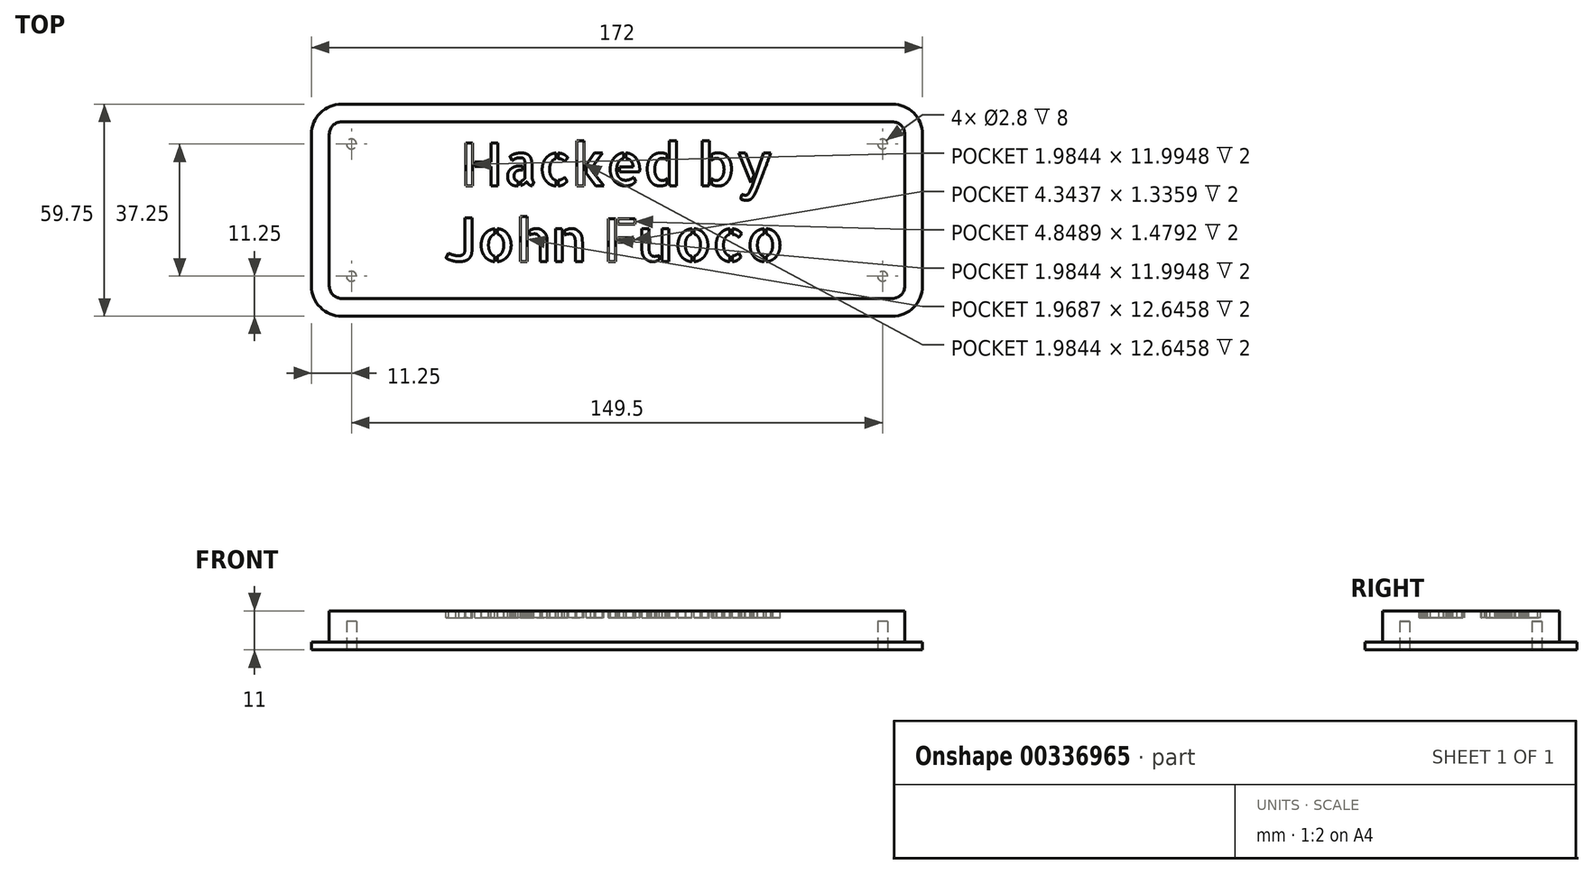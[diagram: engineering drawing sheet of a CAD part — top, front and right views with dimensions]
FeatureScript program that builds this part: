
annotation { "Feature Type Name" : "Feature", "Feature Type Description" : "" }
export const myFeature = defineFeature(function(context is Context, id is Id, definition is map)
    precondition{}
    {
        {
            var Q0;
            Q0=qCreatedBy(makeId("Top.planeOp"),FACE);
            var sketch = newSketch(context, id + "F0", { "sketchPlane" : qUnion([Q0])});
            skLineSegment(sketch, "E0.bottom", {"start": v(3.5, 0) * mm, "end": v(158.5, 0) * mm});
            skLineSegment(sketch, "E0.top", {"start": v(3.5, 49.75) * mm, "end": v(158.5, 49.75) * mm});
            skLineSegment(sketch, "E0.left", {"start": v(0, 3.5) * mm, "end": v(0, 46.25) * mm});
            skLineSegment(sketch, "E0.right", {"start": v(162, 3.5) * mm, "end": v(162, 46.25) * mm});
            skPoint(sketch, "E1.visualSharp", {"position": v(0, 49.75) * mm});
            skArc(sketch, "E1.filletArc", {"start": v(3.5, 49.75) * mm, "mid": v(1.03, 48.72) * mm, "end": v(0, 46.25) * mm});
            skPoint(sketch, "E2.visualSharp", {"position": v(162, 49.75) * mm});
            skArc(sketch, "E2.filletArc", {"start": v(162, 46.25) * mm, "mid": v(160.97, 48.72) * mm, "end": v(158.5, 49.75) * mm});
            skPoint(sketch, "E3.visualSharp", {"position": v(162, 0) * mm});
            skArc(sketch, "E3.filletArc", {"start": v(158.5, 0) * mm, "mid": v(160.97, 1.03) * mm, "end": v(162, 3.5) * mm});
            skPoint(sketch, "E4.visualSharp", {"position": v(0, 0) * mm});
            skArc(sketch, "E4.filletArc", {"start": v(0, 3.5) * mm, "mid": v(1.03, 1.03) * mm, "end": v(3.5, 0) * mm});
            skArc(sketch, "E5.0", {"start": v(3.5, 54.75) * mm, "mid": v(-2.51, 52.26) * mm, "end": v(-5, 46.25) * mm});
            skLineSegment(sketch, "E5.1", {"start": v(-5, 3.5) * mm, "end": v(-5, 46.25) * mm});
            skLineSegment(sketch, "E5.2", {"start": v(3.5, 54.75) * mm, "end": v(158.5, 54.75) * mm});
            skArc(sketch, "E5.3", {"start": v(-5, 3.5) * mm, "mid": v(-2.51, -2.51) * mm, "end": v(3.5, -5) * mm});
            skArc(sketch, "E5.4", {"start": v(167, 46.25) * mm, "mid": v(164.51, 52.26) * mm, "end": v(158.5, 54.75) * mm});
            skLineSegment(sketch, "E5.5", {"start": v(167, 3.5) * mm, "end": v(167, 46.25) * mm});
            skArc(sketch, "E5.6", {"start": v(158.5, -5) * mm, "mid": v(164.51, -2.51) * mm, "end": v(167, 3.5) * mm});
            skLineSegment(sketch, "E5.7", {"start": v(3.5, -5) * mm, "end": v(158.5, -5) * mm});
            skCircle(sketch, "E6", {"center": v(6.25, 6.25) * mm, "radius": 1.4 * mm});
            skCircle(sketch, "E7", {"center": v(6.25, 43.5) * mm, "radius": 1.4 * mm});
            skCircle(sketch, "E8", {"center": v(155.75, 43.5) * mm, "radius": 1.4 * mm});
            skCircle(sketch, "E9", {"center": v(155.75, 6.25) * mm, "radius": 1.4 * mm});
            skSolve(sketch);
        }
        {
            var Q0;
            Q0=makeQuery(id+"F0.imprint","IMPRINT",FACE,{"disambiguationData":[TD([[makeQuery(id+"F0.imprint","IMPRINT",EDGE,{"derivedFrom":sQuery(id+"F0.wireOp",EDGE,"E0.bottom")}),1.0]])]});
            extrude(context, id + "F1", {"entities" : qUnion([Q0]), "depth" : 11 * mm});
        }
        {
            var Q0;
            Q0=makeQuery(id+"F0.imprint","IMPRINT",FACE,{"disambiguationData":[TD([[makeQuery(id+"F0.imprint","IMPRINT",EDGE,{"derivedFrom":sQuery(id+"F0.wireOp",EDGE,"E0.bottom")}),-1.0]])]});
            extrude(context, id + "F2", {"entities" : qUnion([Q0]), "operationType" : NewBodyOperationType.ADD, "depth" : 2.2 * mm});
        }
        {
            var Q0;
            Q0=makeQuery(id+"F0.imprint","IMPRINT",FACE,{"disambiguationData":[TD([[makeQuery(id+"F0.imprint","IMPRINT",EDGE,{"derivedFrom":sQuery(id+"F0.wireOp",EDGE,"E7")}),1.0]])]});
            var Q1;
            Q1=makeQuery(id+"F0.imprint","IMPRINT",FACE,{"disambiguationData":[TD([[makeQuery(id+"F0.imprint","IMPRINT",EDGE,{"derivedFrom":sQuery(id+"F0.wireOp",EDGE,"E6")}),1.0]])]});
            var Q2;
            Q2=makeQuery(id+"F0.imprint","IMPRINT",FACE,{"disambiguationData":[TD([[makeQuery(id+"F0.imprint","IMPRINT",EDGE,{"derivedFrom":sQuery(id+"F0.wireOp",EDGE,"E9")}),1.0]])]});
            var Q3;
            Q3=makeQuery(id+"F0.imprint","IMPRINT",FACE,{"disambiguationData":[TD([[makeQuery(id+"F0.imprint","IMPRINT",EDGE,{"derivedFrom":sQuery(id+"F0.wireOp",EDGE,"E8")}),1.0]])]});
            extrude(context, id + "F3", {"entities" : qUnion([Q0, Q1, Q2, Q3]), "operationType" : NewBodyOperationType.ADD, "depth" : 11 * mm, "hasSecondDirection" : true, "secondDirectionOppositeDirection" : false, "secondDirectionDepth" : 8 * mm});
        }
        {
            var Q0;
            {var subQ0=sQuery(id+"F0.wireOp",EDGE,"E9");var subQ1=sQuery(id+"F0.wireOp",EDGE,"E8");var subQ2=sQuery(id+"F0.wireOp",EDGE,"E7");var subQ3=sQuery(id+"F0.wireOp",EDGE,"E6");Q0=makeQuery(id+"F3.boolean.opBoolean","MERGE",FACE,{"derivedFrom":[makeQuery(id+"F1.opExtrude","CAP_FACE",FACE,{"disambiguationData":[OSD([sQuery(id+"F0.wireOp",EDGE,"E0.bottom"),sQuery(id+"F0.wireOp",EDGE,"E0.top"),sQuery(id+"F0.wireOp",EDGE,"E0.left"),sQuery(id+"F0.wireOp",EDGE,"E0.right"),sQuery(id+"F0.wireOp",EDGE,"E1.filletArc"),sQuery(id+"F0.wireOp",EDGE,"E2.filletArc"),sQuery(id+"F0.wireOp",EDGE,"E3.filletArc"),sQuery(id+"F0.wireOp",EDGE,"E4.filletArc"),subQ3,subQ2,subQ1,subQ0])],"isStart":false}),makeQuery(id+"F3.opExtrude","CAP_FACE",FACE,{"disambiguationData":[OSD([subQ3])],"isStart":false}),makeQuery(id+"F3.opExtrude","CAP_FACE",FACE,{"disambiguationData":[OSD([subQ2])],"isStart":false}),makeQuery(id+"F3.opExtrude","CAP_FACE",FACE,{"disambiguationData":[OSD([subQ1])],"isStart":false}),makeQuery(id+"F3.opExtrude","CAP_FACE",FACE,{"disambiguationData":[OSD([subQ0])],"isStart":false})]});}
            var sketch = newSketch(context, id + "F4", { "sketchPlane" : qUnion([Q0])});
            skText(sketch, "E10", { "text": " Hacked by\nJohn Fuoco", "fontName": "AllertaStencil-Regular.ttf"});
            const initialGuessF4  = {"E10": [0.03238, 0.03175, 1, 0, 0.012]};
            skSetInitialGuess(sketch, initialGuessF4);
            skSolve(sketch);
        }
        {
            var Q0;
            Q0=makeQuery(id+"F4.imprint","IMPRINT",FACE,{"disambiguationData":[TD([[makeQuery(id+"F4.imprint","IMPRINT",EDGE,{"derivedFrom":sQuery(id+"F4.wireOp",EDGE,"E10.sketch_text.stroke-8")}),-1.0]])]});
            var Q1;
            Q1=makeQuery(id+"F4.imprint","IMPRINT",FACE,{"disambiguationData":[TD([[makeQuery(id+"F4.imprint","IMPRINT",EDGE,{"derivedFrom":sQuery(id+"F4.wireOp",EDGE,"E10.sketch_text.stroke-0")}),-1.0]])]});
            var Q2;
            Q2=makeQuery(id+"F4.imprint","IMPRINT",FACE,{"disambiguationData":[TD([[makeQuery(id+"F4.imprint","IMPRINT",EDGE,{"derivedFrom":sQuery(id+"F4.wireOp",EDGE,"E10.sketch_text.stroke-31")}),-1.0]])]});
            var Q3;
            Q3=makeQuery(id+"F4.imprint","IMPRINT",FACE,{"disambiguationData":[TD([[makeQuery(id+"F4.imprint","IMPRINT",EDGE,{"derivedFrom":sQuery(id+"F4.wireOp",EDGE,"E10.sketch_text.stroke-12")}),-1.0]])]});
            var Q4;
            Q4=makeQuery(id+"F4.imprint","IMPRINT",FACE,{"disambiguationData":[TD([[makeQuery(id+"F4.imprint","IMPRINT",EDGE,{"derivedFrom":sQuery(id+"F4.wireOp",EDGE,"E10.sketch_text.stroke-79")}),-1.0]])]});
            var Q5;
            Q5=makeQuery(id+"F4.imprint","IMPRINT",FACE,{"disambiguationData":[TD([[makeQuery(id+"F4.imprint","IMPRINT",EDGE,{"derivedFrom":sQuery(id+"F4.wireOp",EDGE,"E10.sketch_text.stroke-67")}),-1.0]])]});
            var Q6;
            Q6=makeQuery(id+"F4.imprint","IMPRINT",FACE,{"disambiguationData":[TD([[makeQuery(id+"F4.imprint","IMPRINT",EDGE,{"derivedFrom":sQuery(id+"F4.wireOp",EDGE,"E10.sketch_text.stroke-73")}),-1.0]])]});
            var Q7;
            Q7=makeQuery(id+"F4.imprint","IMPRINT",FACE,{"disambiguationData":[TD([[makeQuery(id+"F4.imprint","IMPRINT",EDGE,{"derivedFrom":sQuery(id+"F4.wireOp",EDGE,"E10.sketch_text.stroke-102")}),-1.0]])]});
            var Q8;
            Q8=makeQuery(id+"F4.imprint","IMPRINT",FACE,{"disambiguationData":[TD([[makeQuery(id+"F4.imprint","IMPRINT",EDGE,{"derivedFrom":sQuery(id+"F4.wireOp",EDGE,"E10.sketch_text.stroke-95")}),-1.0]])]});
            var Q9;
            Q9=makeQuery(id+"F4.imprint","IMPRINT",FACE,{"disambiguationData":[TD([[makeQuery(id+"F4.imprint","IMPRINT",EDGE,{"derivedFrom":sQuery(id+"F4.wireOp",EDGE,"E10.sketch_text.stroke-119")}),-1.0]])]});
            var Q10;
            Q10=makeQuery(id+"F4.imprint","IMPRINT",FACE,{"disambiguationData":[TD([[makeQuery(id+"F4.imprint","IMPRINT",EDGE,{"derivedFrom":sQuery(id+"F4.wireOp",EDGE,"E10.sketch_text.stroke-106")}),-1.0]])]});
            var Q11;
            Q11=makeQuery(id+"F4.imprint","IMPRINT",FACE,{"disambiguationData":[TD([[makeQuery(id+"F4.imprint","IMPRINT",EDGE,{"derivedFrom":sQuery(id+"F4.wireOp",EDGE,"E10.sketch_text.stroke-148")}),-1.0]])]});
            var Q12;
            Q12=makeQuery(id+"F4.imprint","IMPRINT",FACE,{"disambiguationData":[TD([[makeQuery(id+"F4.imprint","IMPRINT",EDGE,{"derivedFrom":sQuery(id+"F4.wireOp",EDGE,"E10.sketch_text.stroke-143")}),-1.0]])]});
            var Q13;
            Q13=makeQuery(id+"F4.imprint","IMPRINT",FACE,{"disambiguationData":[TD([[makeQuery(id+"F4.imprint","IMPRINT",EDGE,{"derivedFrom":sQuery(id+"F4.wireOp",EDGE,"E10.sketch_text.stroke-173")}),-1.0]])]});
            var Q14;
            Q14=makeQuery(id+"F4.imprint","IMPRINT",FACE,{"disambiguationData":[TD([[makeQuery(id+"F4.imprint","IMPRINT",EDGE,{"derivedFrom":sQuery(id+"F4.wireOp",EDGE,"E10.sketch_text.stroke-179")}),-1.0]])]});
            var Q15;
            Q15=makeQuery(id+"F4.imprint","IMPRINT",FACE,{"disambiguationData":[TD([[makeQuery(id+"F4.imprint","IMPRINT",EDGE,{"derivedFrom":sQuery(id+"F4.wireOp",EDGE,"E10.sketch_text.stroke-230")}),-1.0]])]});
            var Q16;
            Q16=makeQuery(id+"F4.imprint","IMPRINT",FACE,{"disambiguationData":[TD([[makeQuery(id+"F4.imprint","IMPRINT",EDGE,{"derivedFrom":sQuery(id+"F4.wireOp",EDGE,"E10.sketch_text.stroke-206")}),-1.0]])]});
            var Q17;
            Q17=makeQuery(id+"F4.imprint","IMPRINT",FACE,{"disambiguationData":[TD([[makeQuery(id+"F4.imprint","IMPRINT",EDGE,{"derivedFrom":sQuery(id+"F4.wireOp",EDGE,"E10.sketch_text.stroke-235")}),-1.0]])]});
            var Q18;
            Q18=makeQuery(id+"F4.imprint","IMPRINT",FACE,{"disambiguationData":[TD([[makeQuery(id+"F4.imprint","IMPRINT",EDGE,{"derivedFrom":sQuery(id+"F4.wireOp",EDGE,"E10.sketch_text.stroke-269")}),-1.0]])]});
            var Q19;
            Q19=makeQuery(id+"F4.imprint","IMPRINT",FACE,{"disambiguationData":[TD([[makeQuery(id+"F4.imprint","IMPRINT",EDGE,{"derivedFrom":sQuery(id+"F4.wireOp",EDGE,"E10.sketch_text.stroke-253")}),-1.0]])]});
            var Q20;
            Q20=makeQuery(id+"F4.imprint","IMPRINT",FACE,{"disambiguationData":[TD([[makeQuery(id+"F4.imprint","IMPRINT",EDGE,{"derivedFrom":sQuery(id+"F4.wireOp",EDGE,"E10.sketch_text.stroke-285")}),-1.0]])]});
            var Q21;
            Q21=makeQuery(id+"F4.imprint","IMPRINT",FACE,{"disambiguationData":[TD([[makeQuery(id+"F4.imprint","IMPRINT",EDGE,{"derivedFrom":sQuery(id+"F4.wireOp",EDGE,"E10.sketch_text.stroke-289")}),-1.0]])]});
            var Q22;
            Q22=makeQuery(id+"F4.imprint","IMPRINT",FACE,{"disambiguationData":[TD([[makeQuery(id+"F4.imprint","IMPRINT",EDGE,{"derivedFrom":sQuery(id+"F4.wireOp",EDGE,"E10.sketch_text.stroke-308")}),-1.0]])]});
            var Q23;
            Q23=makeQuery(id+"F4.imprint","IMPRINT",FACE,{"disambiguationData":[TD([[makeQuery(id+"F4.imprint","IMPRINT",EDGE,{"derivedFrom":sQuery(id+"F4.wireOp",EDGE,"E10.sketch_text.stroke-313")}),-1.0]])]});
            var Q24;
            Q24=makeQuery(id+"F4.imprint","IMPRINT",FACE,{"disambiguationData":[TD([[makeQuery(id+"F4.imprint","IMPRINT",EDGE,{"derivedFrom":sQuery(id+"F4.wireOp",EDGE,"E10.sketch_text.stroke-332")}),-1.0]])]});
            var Q25;
            Q25=makeQuery(id+"F4.imprint","IMPRINT",FACE,{"disambiguationData":[TD([[makeQuery(id+"F4.imprint","IMPRINT",EDGE,{"derivedFrom":sQuery(id+"F4.wireOp",EDGE,"E10.sketch_text.stroke-340")}),-1.0]])]});
            var Q26;
            Q26=makeQuery(id+"F4.imprint","IMPRINT",FACE,{"disambiguationData":[TD([[makeQuery(id+"F4.imprint","IMPRINT",EDGE,{"derivedFrom":sQuery(id+"F4.wireOp",EDGE,"E10.sketch_text.stroke-336")}),-1.0]])]});
            var Q27;
            Q27=makeQuery(id+"F4.imprint","IMPRINT",FACE,{"disambiguationData":[TD([[makeQuery(id+"F4.imprint","IMPRINT",EDGE,{"derivedFrom":sQuery(id+"F4.wireOp",EDGE,"E10.sketch_text.stroke-344")}),-1.0]])]});
            var Q28;
            Q28=makeQuery(id+"F4.imprint","IMPRINT",FACE,{"disambiguationData":[TD([[makeQuery(id+"F4.imprint","IMPRINT",EDGE,{"derivedFrom":sQuery(id+"F4.wireOp",EDGE,"E10.sketch_text.stroke-364")}),-1.0]])]});
            var Q29;
            Q29=makeQuery(id+"F4.imprint","IMPRINT",FACE,{"disambiguationData":[TD([[makeQuery(id+"F4.imprint","IMPRINT",EDGE,{"derivedFrom":sQuery(id+"F4.wireOp",EDGE,"E10.sketch_text.stroke-385")}),-1.0]])]});
            var Q30;
            Q30=makeQuery(id+"F4.imprint","IMPRINT",FACE,{"disambiguationData":[TD([[makeQuery(id+"F4.imprint","IMPRINT",EDGE,{"derivedFrom":sQuery(id+"F4.wireOp",EDGE,"E10.sketch_text.stroke-369")}),-1.0]])]});
            var Q31;
            Q31=makeQuery(id+"F4.imprint","IMPRINT",FACE,{"disambiguationData":[TD([[makeQuery(id+"F4.imprint","IMPRINT",EDGE,{"derivedFrom":sQuery(id+"F4.wireOp",EDGE,"E10.sketch_text.stroke-413")}),-1.0]])]});
            var Q32;
            Q32=makeQuery(id+"F4.imprint","IMPRINT",FACE,{"disambiguationData":[TD([[makeQuery(id+"F4.imprint","IMPRINT",EDGE,{"derivedFrom":sQuery(id+"F4.wireOp",EDGE,"E10.sketch_text.stroke-401")}),-1.0]])]});
            var Q33;
            Q33=makeQuery(id+"F4.imprint","IMPRINT",FACE,{"disambiguationData":[TD([[makeQuery(id+"F4.imprint","IMPRINT",EDGE,{"derivedFrom":sQuery(id+"F4.wireOp",EDGE,"E10.sketch_text.stroke-407")}),-1.0]])]});
            var Q34;
            Q34=makeQuery(id+"F4.imprint","IMPRINT",FACE,{"disambiguationData":[TD([[makeQuery(id+"F4.imprint","IMPRINT",EDGE,{"derivedFrom":sQuery(id+"F4.wireOp",EDGE,"E10.sketch_text.stroke-445")}),-1.0]])]});
            var Q35;
            Q35=makeQuery(id+"F4.imprint","IMPRINT",FACE,{"disambiguationData":[TD([[makeQuery(id+"F4.imprint","IMPRINT",EDGE,{"derivedFrom":sQuery(id+"F4.wireOp",EDGE,"E10.sketch_text.stroke-429")}),-1.0]])]});
            extrude(context, id + "F5", {"entities" : qUnion([Q0, Q1, Q2, Q3, Q4, Q5, Q6, Q7, Q8, Q9, Q10, Q11, Q12, Q13, Q14, Q15, Q16, Q17, Q18, Q19, Q20, Q21, Q22, Q23, Q24, Q25, Q26, Q27, Q28, Q29, Q30, Q31, Q32, Q33, Q34, Q35]), "operationType" : NewBodyOperationType.REMOVE, "oppositeDirection" : true, "depth" : 2 * mm});
        }
    });
